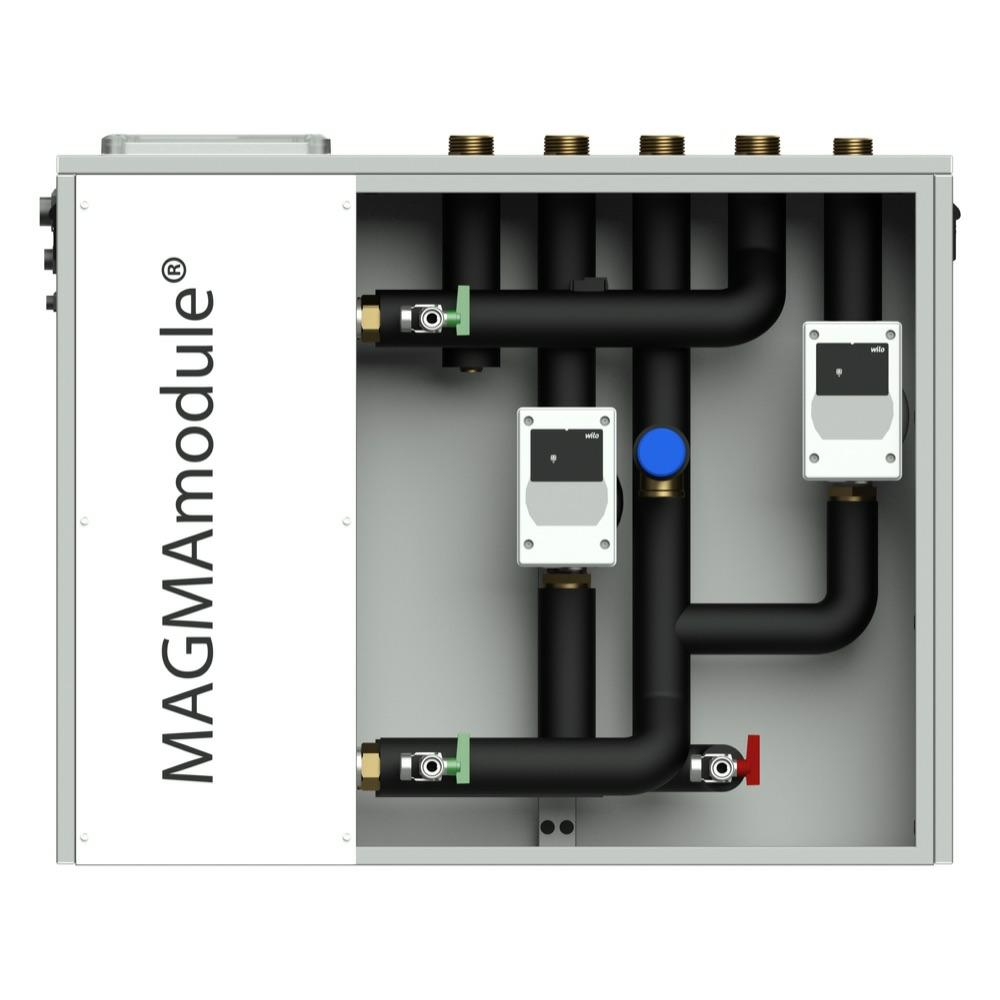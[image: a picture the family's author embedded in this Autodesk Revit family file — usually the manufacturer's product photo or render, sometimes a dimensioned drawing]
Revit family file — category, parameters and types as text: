
# Revit family: Pump station MAGMAmodule® Fresh MEGA (2021)
name_source: partatom
category: Mechanical Equipment
units: mm (PartAtom-declared; Revit-internal decimal feet)

## family parameters
Always vertical = Yes
Classification = Pump
Cut with Voids When Loaded = No
OmniClass Number = 23.75.00.00
OmniClass Title = Climate Control (HVAC)
Part Type = Normal
Room Calculation Point = No
Round Connector Dimension = Use Diameter
Shared = Yes
Work Plane-Based = No

## types (1)
- Pump station MAGMAmodule® Fresh MEGA (2021)
    Assembly Code = F0120150R
    Data revision = 21.02.2024
    Default Elevation = 0 mm  [stored 0 ft]
    Description = Автоматична станція гарячого водопостачання | До 200 літрів гарячої води на хвилину

У ємнісних баках-водонагрівачах питної води в процесі експлуатації можуть розвиватися небезпечні для здоров’я легіонели, бактерії та мікроби. Вирішенням цієї проблеми є станції гарячого водопостачання MAGMAmodule® Fresh. Станції спроєктовані шляхом інтеграції передових технологій сфер гідравліки та електроніки. Електронне управління забезпечує швидке та стабільне виробництво гарячої води, а пластинчатий теплообмінник із нержавіючої сталі відмінну гігієнічність. Нагрів води здійснюється теплоносієм буферної ємності, яка може нагріватися будь-якими теплогенераторами (газовий котел, електрика, тепловий насос, геліосистема …).

MAGMAmodule® Fresh MEGA продуктивністю до 200 літрів за хвилину може об’єднуватися в каскад до 6 модулів з загальною продуктивністю гарячої води до 1200 літрів за хвилину. Ідеально підходить для комерційних об’єктів та підприємств з чималим споживанням гарячої води.
Кожен модуль за запитом може оснащуватися системою дистанційного керування та моніторингу.
    Model = MAGMAmodule® Fresh MEGA
    Revit/family revision = revit-2021/family-1.1
    Type Image = magmamodule-fresh-mega-150.jpeg
    URL = https://www.magmaenergy.com.ua
    YouTube = https://www.youtube.com
    d1_Т3 = 40 mm  [stored 0.131234 ft]
    d2_Т4 = 32 mm  [stored 0.104987 ft]
    d3_В1 = 40 mm  [stored 0.131234 ft]
    d4_Т1 = 40 mm  [stored 0.131234 ft]
    d5_Т2 = 40 mm  [stored 0.131234 ft]
    r1 = 20 mm  [stored 0.0656168 ft]
    r2 = 16 mm  [stored 0.0524934 ft]
    r3 = 20 mm  [stored 0.0656168 ft]
    r4 = 20 mm  [stored 0.0656168 ft]
    r5 = 20 mm  [stored 0.0656168 ft]
    Напруга = 230 В
    Споживана потужність = 350 Вт
    Струм = 2 А

note: [stored X ft] marks values corroborated as IEEE doubles in the binary element streams (Revit-internal decimal feet)

## geometry (parser evidence)
native form markers: Sweep x3
no freeform markers — native parametric forms only
